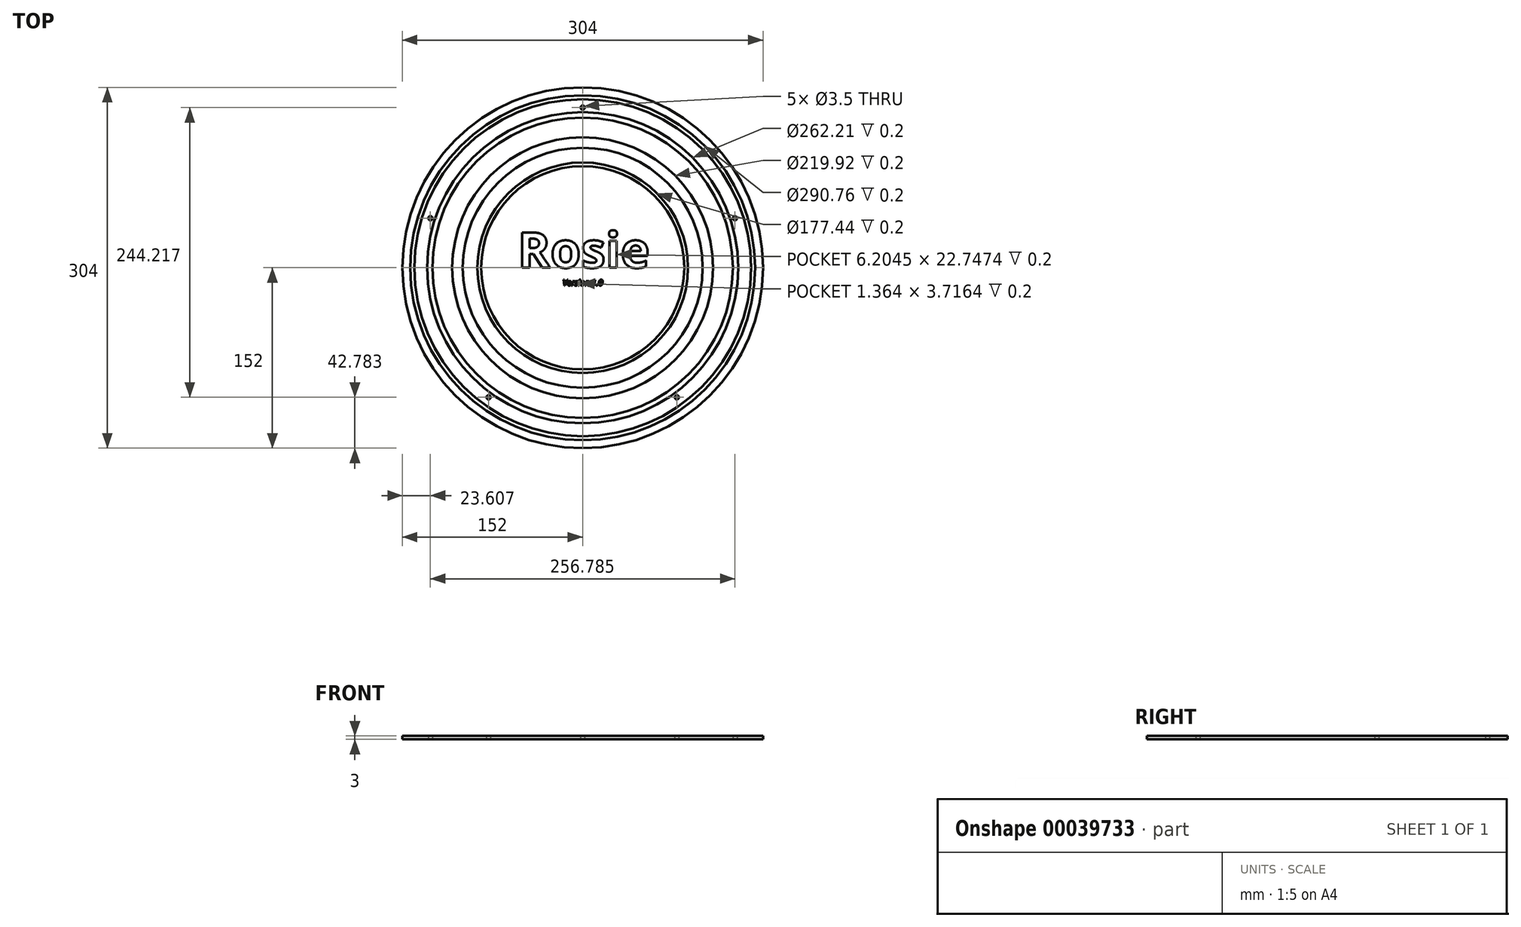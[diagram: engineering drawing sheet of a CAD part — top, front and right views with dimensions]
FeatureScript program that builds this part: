
annotation { "Feature Type Name" : "Feature", "Feature Type Description" : "" }
export const myFeature = defineFeature(function(context is Context, id is Id, definition is map)
    precondition{}
    {
        {
            var Q0;
            Q0=qCreatedBy(makeId("Top.planeOp"),FACE);
            var sketch = newSketch(context, id + "F0", { "sketchPlane" : qUnion([Q0])});
            skCircle(sketch, "E0", {"center": v(0, 0) * mm, "radius": 152 * mm});
            skCircle(sketch, "E1.cCircle", {"center": v(0, 0) * mm, "radius": 135 * mm, "construction": true});
            skLineSegment(sketch, "E1.0", {"start": v(0, 135) * mm, "end": v(128.4, 41.72) * mm, "construction": true});
            skLineSegment(sketch, "E1.1", {"start": v(128.4, 41.72) * mm, "end": v(79.35, -109.22) * mm, "construction": true});
            skLineSegment(sketch, "E1.2", {"start": v(79.35, -109.22) * mm, "end": v(-79.35, -109.22) * mm, "construction": true});
            skLineSegment(sketch, "E1.3", {"start": v(-79.35, -109.22) * mm, "end": v(-128.4, 41.72) * mm, "construction": true});
            skLineSegment(sketch, "E1.4", {"start": v(-128.4, 41.72) * mm, "end": v(0, 135) * mm, "construction": true});
            skCircle(sketch, "E2", {"center": v(0, 135) * mm, "radius": 1.75 * mm});
            skCircle(sketch, "E3", {"center": v(128.4, 41.72) * mm, "radius": 1.75 * mm});
            skCircle(sketch, "E4", {"center": v(79.35, -109.22) * mm, "radius": 1.75 * mm});
            skCircle(sketch, "E5", {"center": v(-79.35, -109.22) * mm, "radius": 1.75 * mm});
            skCircle(sketch, "E6", {"center": v(-128.4, 41.72) * mm, "radius": 1.75 * mm});
            skLineSegment(sketch, "E7", {"start": v(0, 152) * mm, "end": v(0, 0) * mm, "construction": true});
            skSolve(sketch);
        }
        {
            var Q0;
            Q0 = qSketchRegion(id + "F0", true);
            extrude(context, id + "F1", {"entities" : qUnion([Q0]), "depth" : 3 * mm});
        }
        {
            var Q0;
            Q0=makeQuery(id+"F1.opExtrude","CAP_FACE",FACE,{"disambiguationData":[OSD([sQuery(id+"F0.wireOp",EDGE,"E0"),sQuery(id+"F0.wireOp",EDGE,"E2"),sQuery(id+"F0.wireOp",EDGE,"E3"),sQuery(id+"F0.wireOp",EDGE,"E4"),sQuery(id+"F0.wireOp",EDGE,"E5"),sQuery(id+"F0.wireOp",EDGE,"E6")])],"isStart":false});
            var sketch = newSketch(context, id + "F2", { "sketchPlane" : qUnion([Q0])});
            skText(sketch, "E8", { "text": "Rosie", "fontName": "OpenSans-Bold.ttf"});
            skText(sketch, "E9", { "text": "Version 1.0", "fontName": "OpenSans-Italic.ttf"});
            skLineSegment(sketch, "E10", {"start": v(0, -15) * mm, "end": v(0, 152) * mm, "construction": true});
            skCircle(sketch, "E11", {"center": v(0, 0) * mm, "radius": 85.64 * mm});
            skCircle(sketch, "E12", {"center": v(0, 0) * mm, "radius": 101.12 * mm});
            skCircle(sketch, "E13", {"center": v(0, 0) * mm, "radius": 109.96 * mm});
            skCircle(sketch, "E14", {"center": v(0, 0) * mm, "radius": 126.6 * mm});
            skCircle(sketch, "E15", {"center": v(0, 0) * mm, "radius": 131.1 * mm});
            skCircle(sketch, "E16", {"center": v(0, 0) * mm, "radius": 141.96 * mm});
            skCircle(sketch, "E17", {"center": v(0, 0) * mm, "radius": 145.38 * mm});
            skCircle(sketch, "E18", {"center": v(0, 0) * mm, "radius": 88.72 * mm});
            const initialGuessF2  = {"E8": [-0.05478, 0, 1, 0, 0.03], "E9": [-0.01685, -0.015, 1, 0, 0.005]};
            skSetInitialGuess(sketch, initialGuessF2);
            skSolve(sketch);
        }
        {
            var Q0;
            Q0=makeQuery(id+"F2.imprint","IMPRINT",FACE,{"disambiguationData":[TD([[makeQuery(id+"F2.imprint","IMPRINT",EDGE,{"derivedFrom":sQuery(id+"F2.wireOp",EDGE,"E11")}),-1.0]])]});
            var Q1;
            Q1=makeQuery(id+"F2.imprint","IMPRINT",FACE,{"disambiguationData":[TD([[makeQuery(id+"F2.imprint","IMPRINT",EDGE,{"derivedFrom":sQuery(id+"F2.wireOp",EDGE,"E12")}),-1.0]])]});
            var Q2;
            Q2=makeQuery(id+"F2.imprint","IMPRINT",FACE,{"disambiguationData":[TD([[makeQuery(id+"F2.imprint","IMPRINT",EDGE,{"derivedFrom":sQuery(id+"F2.wireOp",EDGE,"E14")}),-1.0]])]});
            var Q3;
            Q3=makeQuery(id+"F2.imprint","IMPRINT",FACE,{"disambiguationData":[TD([[makeQuery(id+"F2.imprint","IMPRINT",EDGE,{"derivedFrom":sQuery(id+"F2.wireOp",EDGE,"E16")}),-1.0]])]});
            var Q4;
            Q4=makeQuery(id+"F2.imprint","IMPRINT",FACE,{"disambiguationData":[TD([[makeQuery(id+"F2.imprint","IMPRINT",EDGE,{"derivedFrom":sQuery(id+"F2.wireOp",EDGE,"E8.sketch_text.stroke-72")}),-1.0]])]});
            var Q5;
            Q5=makeQuery(id+"F2.imprint","IMPRINT",FACE,{"disambiguationData":[TD([[makeQuery(id+"F2.imprint","IMPRINT",EDGE,{"derivedFrom":sQuery(id+"F2.wireOp",EDGE,"E8.sketch_text.stroke-68")}),-1.0]])]});
            var Q6;
            Q6=makeQuery(id+"F2.imprint","IMPRINT",FACE,{"disambiguationData":[TD([[makeQuery(id+"F2.imprint","IMPRINT",EDGE,{"derivedFrom":sQuery(id+"F2.wireOp",EDGE,"E8.sketch_text.stroke-63")}),-1.0]])]});
            var Q7;
            Q7=makeQuery(id+"F2.imprint","IMPRINT",FACE,{"disambiguationData":[TD([[makeQuery(id+"F2.imprint","IMPRINT",EDGE,{"derivedFrom":sQuery(id+"F2.wireOp",EDGE,"E8.sketch_text.stroke-37")}),-1.0]])]});
            var Q8;
            Q8=makeQuery(id+"F2.imprint","IMPRINT",FACE,{"disambiguationData":[TD([[makeQuery(id+"F2.imprint","IMPRINT",EDGE,{"derivedFrom":sQuery(id+"F2.wireOp",EDGE,"E8.sketch_text.stroke-19")}),-1.0]])]});
            var Q9;
            Q9=makeQuery(id+"F2.imprint","IMPRINT",FACE,{"disambiguationData":[TD([[makeQuery(id+"F2.imprint","IMPRINT",EDGE,{"derivedFrom":sQuery(id+"F2.wireOp",EDGE,"E8.sketch_text.stroke-0")}),-1.0]])]});
            var Q10;
            Q10=makeQuery(id+"F2.imprint","IMPRINT",FACE,{"disambiguationData":[TD([[makeQuery(id+"F2.imprint","IMPRINT",EDGE,{"derivedFrom":sQuery(id+"F2.wireOp",EDGE,"E9.sketch_text.stroke-0")}),-1.0]])]});
            var Q11;
            Q11=makeQuery(id+"F2.imprint","IMPRINT",FACE,{"disambiguationData":[TD([[makeQuery(id+"F2.imprint","IMPRINT",EDGE,{"derivedFrom":sQuery(id+"F2.wireOp",EDGE,"E9.sketch_text.stroke-10")}),-1.0]])]});
            var Q12;
            Q12=makeQuery(id+"F2.imprint","IMPRINT",FACE,{"disambiguationData":[TD([[makeQuery(id+"F2.imprint","IMPRINT",EDGE,{"derivedFrom":sQuery(id+"F2.wireOp",EDGE,"E9.sketch_text.stroke-35")}),-1.0]])]});
            var Q13;
            Q13=makeQuery(id+"F2.imprint","IMPRINT",FACE,{"disambiguationData":[TD([[makeQuery(id+"F2.imprint","IMPRINT",EDGE,{"derivedFrom":sQuery(id+"F2.wireOp",EDGE,"E9.sketch_text.stroke-50")}),-1.0]])]});
            var Q14;
            Q14=makeQuery(id+"F2.imprint","IMPRINT",FACE,{"disambiguationData":[TD([[makeQuery(id+"F2.imprint","IMPRINT",EDGE,{"derivedFrom":sQuery(id+"F2.wireOp",EDGE,"E9.sketch_text.stroke-75")}),-1.0]])]});
            var Q15;
            Q15=makeQuery(id+"F2.imprint","IMPRINT",FACE,{"disambiguationData":[TD([[makeQuery(id+"F2.imprint","IMPRINT",EDGE,{"derivedFrom":sQuery(id+"F2.wireOp",EDGE,"E9.sketch_text.stroke-79")}),-1.0]])]});
            var Q16;
            Q16=makeQuery(id+"F2.imprint","IMPRINT",FACE,{"disambiguationData":[TD([[makeQuery(id+"F2.imprint","IMPRINT",EDGE,{"derivedFrom":sQuery(id+"F2.wireOp",EDGE,"E9.sketch_text.stroke-106")}),-1.0]])]});
            var Q17;
            Q17=makeQuery(id+"F2.imprint","IMPRINT",FACE,{"disambiguationData":[TD([[makeQuery(id+"F2.imprint","IMPRINT",EDGE,{"derivedFrom":sQuery(id+"F2.wireOp",EDGE,"E9.sketch_text.stroke-143")}),-1.0]])]});
            var Q18;
            Q18=makeQuery(id+"F2.imprint","IMPRINT",FACE,{"disambiguationData":[TD([[makeQuery(id+"F2.imprint","IMPRINT",EDGE,{"derivedFrom":sQuery(id+"F2.wireOp",EDGE,"E9.sketch_text.stroke-135")}),-1.0]])]});
            var Q19;
            Q19=makeQuery(id+"F2.imprint","IMPRINT",FACE,{"disambiguationData":[TD([[makeQuery(id+"F2.imprint","IMPRINT",EDGE,{"derivedFrom":sQuery(id+"F2.wireOp",EDGE,"E9.sketch_text.stroke-126")}),-1.0]])]});
            var Q20;
            Q20=makeQuery(id+"F2.imprint","IMPRINT",FACE,{"disambiguationData":[TD([[makeQuery(id+"F2.imprint","IMPRINT",EDGE,{"derivedFrom":sQuery(id+"F2.wireOp",EDGE,"E9.sketch_text.stroke-86")}),-1.0]])]});
            extrude(context, id + "F3", {"entities" : qUnion([Q0, Q1, Q2, Q3, Q4, Q5, Q6, Q7, Q8, Q9, Q10, Q11, Q12, Q13, Q14, Q15, Q16, Q17, Q18, Q19, Q20]), "operationType" : NewBodyOperationType.REMOVE, "oppositeDirection" : true, "depth" : 0.2 * mm});
        }
    });
